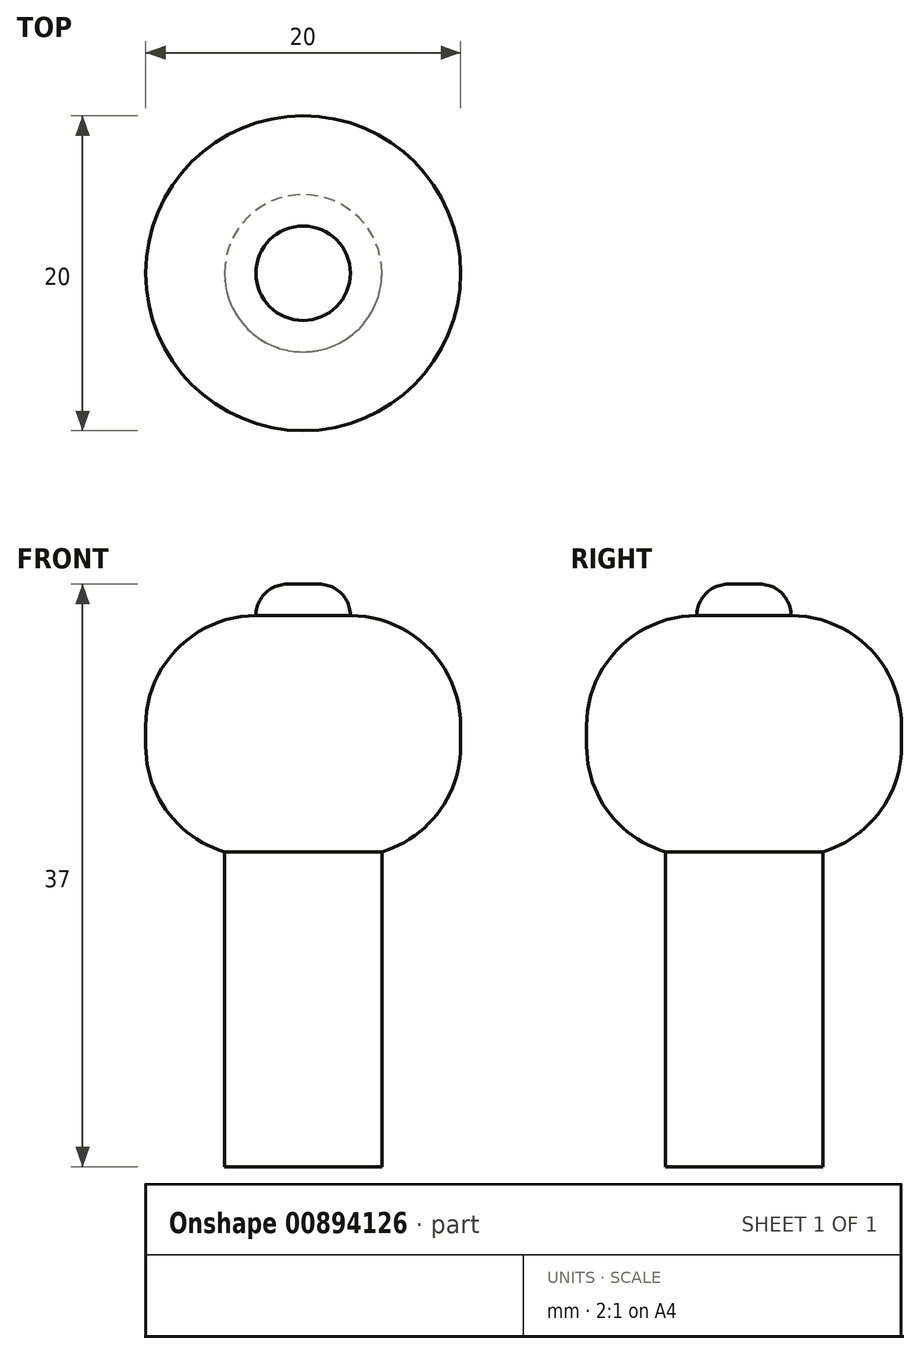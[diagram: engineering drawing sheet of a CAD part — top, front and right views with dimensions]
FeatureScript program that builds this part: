
annotation { "Feature Type Name" : "Feature", "Feature Type Description" : "" }
export const myFeature = defineFeature(function(context is Context, id is Id, definition is map)
    precondition{}
    {
        {
            var Q0;
            Q0=qCreatedBy(makeId("Top.planeOp"),FACE);
            var sketch = newSketch(context, id + "F0", { "sketchPlane" : qUnion([Q0])});
            skCircle(sketch, "E0", {"center": v(0, 0) * mm, "radius": 5 * mm});
            skSolve(sketch);
        }
        {
            var Q0;
            Q0=makeQuery(id+"F0.imprint","IMPRINT",FACE,{"disambiguationData":[TD([[makeQuery(id+"F0.imprint","IMPRINT",EDGE,{"derivedFrom":sQuery(id+"F0.wireOp",EDGE,"E0")}),1.0]])]});
            extrude(context, id + "F1", {"entities" : qUnion([Q0]), "depth" : 20 * mm, "offsetDistance" : 25 * mm});
        }
        {
            var Q0;
            Q0=makeQuery(id+"F1.opExtrude","CAP_FACE",FACE,{"disambiguationData":[OSD([sQuery(id+"F0.wireOp",EDGE,"E0")])],"isStart":false});
            var sketch = newSketch(context, id + "F2", { "sketchPlane" : qUnion([Q0])});
            skCircle(sketch, "E1", {"center": v(0, 0) * mm, "radius": 10 * mm});
            skSolve(sketch);
        }
        {
            var Q0;
            Q0=makeQuery(id+"F2.imprint","IMPRINT",FACE,{"disambiguationData":[TD([[makeQuery(id+"F2.imprint","IMPRINT",EDGE,{"derivedFrom":sQuery(id+"F2.wireOp",EDGE,"E1")}),1.0]])]});
            var Q1;
            Q1=makeQuery(id+"F2.imprint","IMPRINT",FACE,{"disambiguationData":[TD([[makeQuery(id+"F2.imprint","IMPRINT",EDGE,{"derivedFrom":makeQuery(id+"F1.opExtrude","CAP_EDGE",EDGE,{"disambiguationData":[OSD([sQuery(id+"F0.wireOp",EDGE,"E0")])],"isStart":false})}),1.0]])]});
            extrude(context, id + "F3", {"entities" : qUnion([Q0, Q1]), "operationType" : NewBodyOperationType.ADD, "depth" : 15 * mm, "offsetDistance" : 25 * mm});
        }
        {
            var Q0;
            Q0=makeQuery(id+"F3.opExtrude","CAP_EDGE",EDGE,{"disambiguationData":[OSD([sQuery(id+"F2.wireOp",EDGE,"E1")])],"isStart":false});
            var Q1;
            Q1=makeQuery(id+"F3.opExtrude","CAP_EDGE",EDGE,{"disambiguationData":[OSD([sQuery(id+"F2.wireOp",EDGE,"E1")])],"isStart":true});
            fillet(context, id + "F4", {"entities" : qUnion([Q0, Q1]), "radius" : 7 * mm, "tangentPropagation" : true, "allowEdgeOverflow" : false});
        }
        {
            var Q0;
            Q0=makeQuery(id+"F3.opExtrude","CAP_FACE",FACE,{"disambiguationData":[OSD([sQuery(id+"F2.wireOp",EDGE,"E1")])],"isStart":false});
            extrude(context, id + "F5", {"entities" : qUnion([Q0]), "operationType" : NewBodyOperationType.ADD, "depth" : 2 * mm, "offsetDistance" : 25 * mm});
        }
        {
            var Q0;
            Q0=makeQuery(id+"F5.opExtrude","CAP_FACE",FACE,{"disambiguationData":[OSD([sQuery(id+"F2.wireOp",EDGE,"E1")])],"isStart":false});
            fillet(context, id + "F6", {"entities" : qUnion([Q0]), "radius" : 2 * mm, "tangentPropagation" : true, "allowEdgeOverflow" : false});
        }
    });
